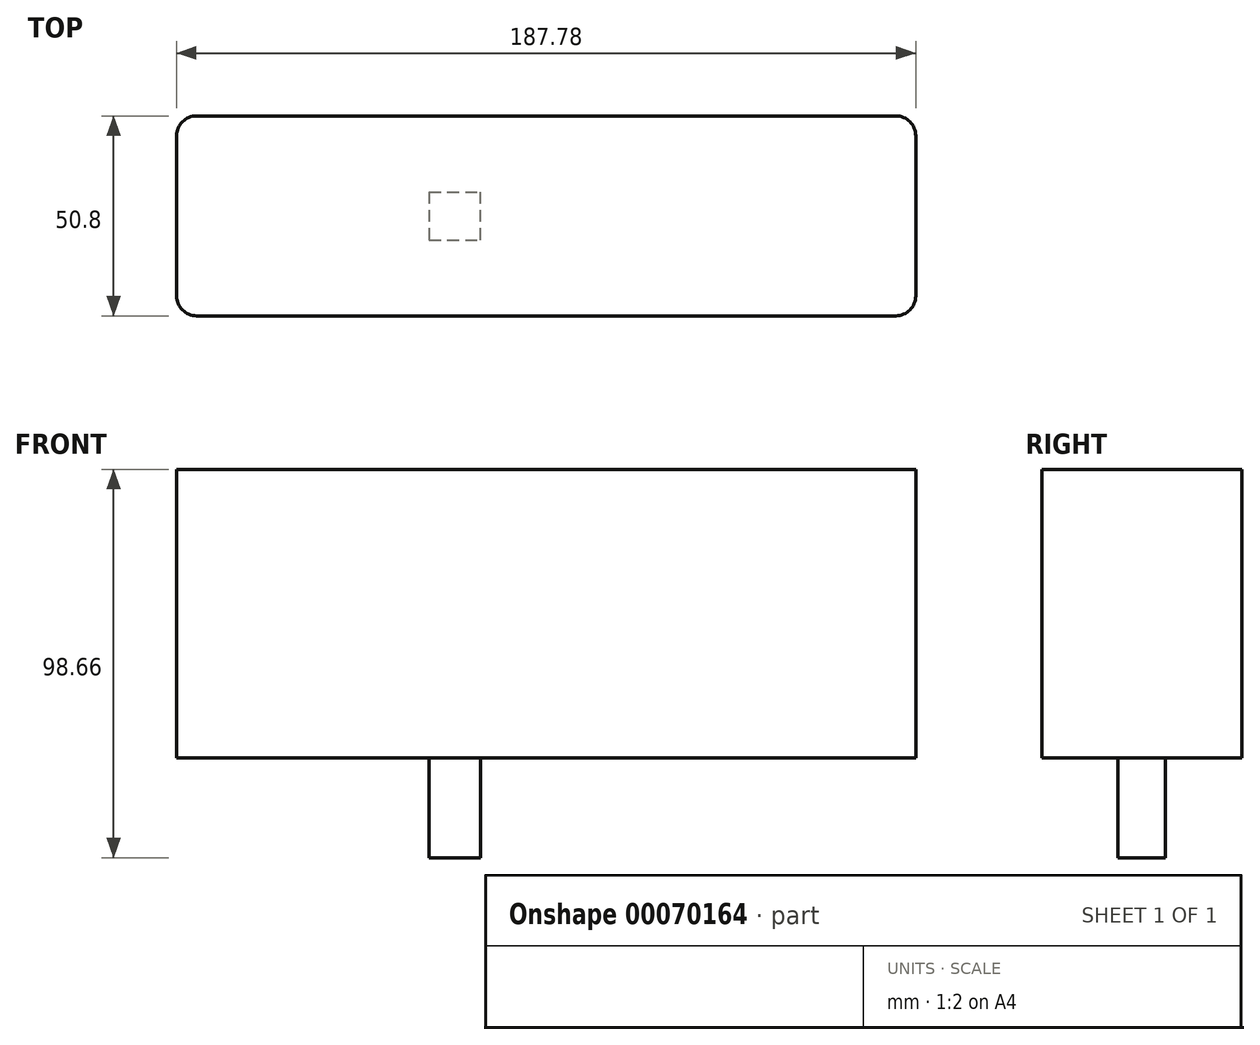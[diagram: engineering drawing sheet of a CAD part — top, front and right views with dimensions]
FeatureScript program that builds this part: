
annotation { "Feature Type Name" : "Feature", "Feature Type Description" : "" }
export const myFeature = defineFeature(function(context is Context, id is Id, definition is map)
    precondition{}
    {
        {
            var Q0;
            Q0=qCreatedBy(makeId("Front.planeOp"),FACE);
            var sketch = newSketch(context, id + "F0", { "sketchPlane" : qUnion([Q0])});
            skLineSegment(sketch, "E0.rect.bottom", {"start": v(-93.89, 36.63) * mm, "end": v(93.89, 36.63) * mm});
            skLineSegment(sketch, "E0.rect.top", {"start": v(-93.89, -36.63) * mm, "end": v(93.89, -36.63) * mm});
            skLineSegment(sketch, "E0.rect.left", {"start": v(-93.89, 36.63) * mm, "end": v(-93.89, -36.63) * mm});
            skLineSegment(sketch, "E0.rect.right", {"start": v(93.89, 36.63) * mm, "end": v(93.89, -36.63) * mm});
            skPoint(sketch, "E0.rect.middle", {"position": v(0, 0) * mm});
            skSolve(sketch);
        }
        {
            var Q0;
            Q0=makeQuery(id+"F0.imprint","IMPRINT",FACE,{"disambiguationData":[TD([[makeQuery(id+"F0.imprint","IMPRINT",EDGE,{"derivedFrom":sQuery(id+"F0.wireOp",EDGE,"E0.rect.bottom")}),-1.0]])]});
            extrude(context, id + "F1", {"entities" : qUnion([Q0]), "endBound" : BoundingType.SYMMETRIC, "depth" : 50.8 * mm});
        }
        {
            var Q0;
            Q0=makeQuery(id+"F1.opExtrude","CAP_EDGE",EDGE,{"disambiguationData":[OSD([sQuery(id+"F0.wireOp",EDGE,"E0.rect.right")])],"isStart":false});
            var Q1;
            Q1=makeQuery(id+"F1.opExtrude","CAP_EDGE",EDGE,{"disambiguationData":[OSD([sQuery(id+"F0.wireOp",EDGE,"E0.rect.right")])],"isStart":true});
            var Q2;
            Q2=makeQuery(id+"F1.opExtrude","CAP_EDGE",EDGE,{"disambiguationData":[OSD([sQuery(id+"F0.wireOp",EDGE,"E0.rect.left")])],"isStart":false});
            var Q3;
            Q3=makeQuery(id+"F1.opExtrude","CAP_EDGE",EDGE,{"disambiguationData":[OSD([sQuery(id+"F0.wireOp",EDGE,"E0.rect.left")])],"isStart":true});
            fillet(context, id + "F2", {"entities" : qUnion([Q0, Q1, Q2, Q3]), "radius" : 5.08 * mm, "tangentPropagation" : true, "allowEdgeOverflow" : false});
        }
        {
            var Q0;
            Q0=makeQuery(id+"F1.opExtrude","SWEPT_FACE",FACE,{"disambiguationData":[OSD([sQuery(id+"F0.wireOp",EDGE,"E0.rect.top")])]});
            var sketch = newSketch(context, id + "F3", { "sketchPlane" : qUnion([Q0])});
            skLineSegment(sketch, "E1.rect.bottom", {"start": v(-58.06, 6.09) * mm, "end": v(-16.71, 6.09) * mm});
            skLineSegment(sketch, "E1.rect.top", {"start": v(-58.06, -6.09) * mm, "end": v(-16.71, -6.09) * mm});
            skLineSegment(sketch, "E1.rect.left", {"start": v(-58.06, 6.09) * mm, "end": v(-58.06, -6.09) * mm});
            skLineSegment(sketch, "E1.rect.right", {"start": v(-16.71, 6.09) * mm, "end": v(-16.71, -6.09) * mm});
            skPoint(sketch, "E1.rect.middle", {"position": v(-37.39, 0) * mm});
            skLineSegment(sketch, "E2.rect.bottom", {"start": v(-45.03, -6.09) * mm, "end": v(-29.74, -6.09) * mm});
            skLineSegment(sketch, "E2.rect.top", {"start": v(-45.03, 6.09) * mm, "end": v(-29.74, 6.09) * mm});
            skLineSegment(sketch, "E2.rect.left", {"start": v(-45.03, -6.09) * mm, "end": v(-45.03, 6.09) * mm});
            skLineSegment(sketch, "E2.rect.right", {"start": v(-29.74, -6.09) * mm, "end": v(-29.74, 6.09) * mm});
            skPoint(sketch, "E3", {"position": v(-82.7, 14.87) * mm});
            skPoint(sketch, "E4.MirrorP", {"position": v(-82.7, -14.87) * mm});
            skPoint(sketch, "E5.MirrorP", {"position": v(82.7, 14.87) * mm});
            skPoint(sketch, "E6.MirrorP", {"position": v(82.7, -14.87) * mm});
            skSolve(sketch);
        }
        {
            var Q0;
            {var subQ0=sQuery(id+"F3.wireOp",EDGE,"E1.rect.right");Q0=makeQuery(id+"F3.imprint","IMPRINT",FACE,{"disambiguationData":[TD([[makeQuery(id+"F3.imprint","IMPRINT",EDGE,{"derivedFrom":subQ0}),-1.0]])]});}
            extrude(context, id + "F4", {"entities" : qUnion([Q0]), "operationType" : NewBodyOperationType.ADD, "depth" : 25.4 * mm});
        }
    });
